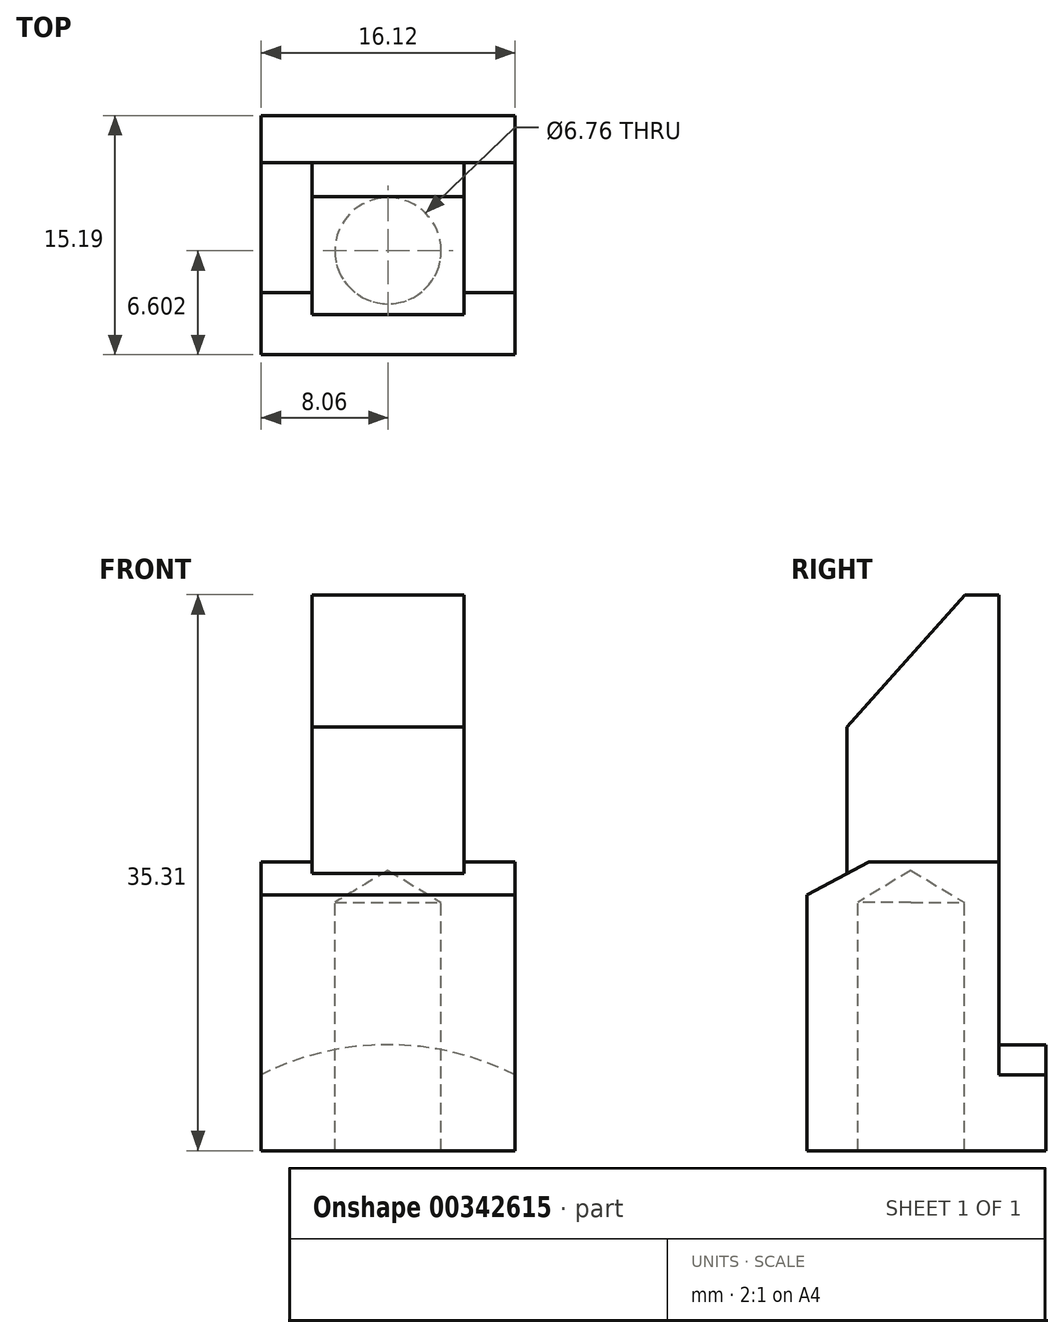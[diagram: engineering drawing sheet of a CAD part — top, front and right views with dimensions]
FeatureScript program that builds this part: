
annotation { "Feature Type Name" : "Feature", "Feature Type Description" : "" }
export const myFeature = defineFeature(function(context is Context, id is Id, definition is map)
    precondition{}
    {
        {
            var Q0;
            Q0=qCreatedBy(makeId("Front.planeOp"),FACE);
            var sketch = newSketch(context, id + "F0", { "sketchPlane" : qUnion([Q0])});
            skLineSegment(sketch, "E0.bottom", {"start": v(-4.83, 35.3) * mm, "end": v(4.83, 35.3) * mm});
            skLineSegment(sketch, "E0.top", {"start": v(-8.06, 0) * mm, "end": v(8.06, 0) * mm});
            skLineSegment(sketch, "E0.left", {"start": v(-8.06, 18.34) * mm, "end": v(-8.06, 0) * mm});
            skLineSegment(sketch, "E0.right", {"start": v(8.06, 18.34) * mm, "end": v(8.06, 0) * mm});
            skLineSegment(sketch, "E1", {"start": v(-8.06, 18.34) * mm, "end": v(8.06, 18.34) * mm});
            skLineSegment(sketch, "E2", {"start": v(4.83, 35.3) * mm, "end": v(4.83, 18.34) * mm});
            skLineSegment(sketch, "E3", {"start": v(-4.83, 35.3) * mm, "end": v(-4.83, 18.34) * mm});
            skLineSegment(sketch, "E4", {"start": v(-4.83, 35.3) * mm, "end": v(4.83, 18.34) * mm, "construction": true});
            skLineSegment(sketch, "E5", {"start": v(0, 26.82) * mm, "end": v(0, 0) * mm, "construction": true});
            skPoint(sketch, "E5.startSnap0", {"position": v(0, 26.82) * mm});
            skArc(sketch, "E6", {"start": v(8.06, 4.83) * mm, "mid": v(0, 6.73) * mm, "end": v(-8.06, 4.83) * mm});
            skLineSegment(sketch, "E7", {"start": v(0, 0) * mm, "end": v(0, -11.3) * mm, "construction": true});
            skSolve(sketch);
        }
        {
            var Q0;
            Q0 = qSketchRegion(id + "F0", true);
            extrude(context, id + "F1", {"entities" : qUnion([Q0]), "depth" : 12.2 * mm});
        }
        {
            var Q0;
            {var subQ0=sQuery(id+"F0.wireOp",EDGE,"E0.top");Q0=makeQuery(id+"F0.imprint","IMPRINT",FACE,{"disambiguationData":[TD([[makeQuery(id+"F0.imprint","IMPRINT",EDGE,{"derivedFrom":subQ0}),1.0]])]});}
            extrude(context, id + "F2", {"entities" : qUnion([Q0]), "operationType" : NewBodyOperationType.ADD, "oppositeDirection" : true, "depth" : 3 * mm});
        }
        {
            var Q0;
            Q0=makeQuery(id+"F1.opExtrude","SWEPT_FACE",FACE,{"disambiguationData":[OSD([sQuery(id+"F0.wireOp",EDGE,"E3")])]});
            var sketch = newSketch(context, id + "F3", { "sketchPlane" : qUnion([Q0])});
            skLineSegment(sketch, "E8", {"start": v(2.16, 35.3) * mm, "end": v(9.65, 26.92) * mm});
            skLineSegment(sketch, "E9", {"start": v(9.65, 26.92) * mm, "end": v(15.1, 26.92) * mm, "construction": true});
            skLineSegment(sketch, "E10", {"start": v(15.1, 26.92) * mm, "end": v(15.1, 37.65) * mm});
            skLineSegment(sketch, "E11", {"start": v(15.1, 37.65) * mm, "end": v(2.16, 37.65) * mm});
            skLineSegment(sketch, "E12", {"start": v(2.16, 37.65) * mm, "end": v(2.16, 35.3) * mm});
            skLineSegment(sketch, "E13", {"start": v(9.65, 26.92) * mm, "end": v(9.65, 17.6) * mm});
            skLineSegment(sketch, "E14", {"start": v(9.65, 17.6) * mm, "end": v(12.2, 16.26) * mm});
            skLineSegment(sketch, "E15", {"start": v(9.65, 17.6) * mm, "end": v(8.26, 18.34) * mm});
            skLineSegment(sketch, "E16", {"start": v(12.2, 16.26) * mm, "end": v(15.1, 16.26) * mm});
            skLineSegment(sketch, "E17", {"start": v(15.1, 16.26) * mm, "end": v(15.1, 26.92) * mm});
            skLineSegment(sketch, "E18.0", {"start": v(12.2, 18.34) * mm, "end": v(12.2, 0) * mm, "construction": true});
            skSolve(sketch);
        }
        {
            var Q0;
            Q0 = qSketchRegion(id + "F3", true);
            extrude(context, id + "F4", {"entities" : qUnion([Q0]), "operationType" : NewBodyOperationType.REMOVE, "oppositeDirection" : true, "depth" : 50.8 * mm, "symmetric" : true});
        }
        {
            var Q0;
            {var subQ3=sQuery(id+"F3.wireOp",EDGE,"E8");Q0=makeQuery(id+"F3.imprint","IMPRINT",FACE,{"disambiguationData":[TD([[makeQuery(id+"F3.imprint","IMPRINT",EDGE,{"derivedFrom":subQ3}),-1.0]])]});}
            var sketch = newSketch(context, id + "F5", { "sketchPlane" : qUnion([Q0])});
            skLineSegment(sketch, "E19.0", {"start": v(9.65, 18.34) * mm, "end": v(8.26, 18.34) * mm});
            skPoint(sketch, "E20.0", {"position": v(8.95, 17.97) * mm});
            skLineSegment(sketch, "E21.0", {"start": v(9.65, 18.34) * mm, "end": v(9.65, 17.6) * mm});
            skPoint(sketch, "E22.orphan", {"position": v(9.65, 26.92) * mm});
            skLineSegment(sketch, "E23.0", {"start": v(9.65, 17.6) * mm, "end": v(8.26, 18.34) * mm});
            skPoint(sketch, "E24.orphan", {"position": v(0, 18.34) * mm});
            skSolve(sketch);
        }
        {
            var Q0;
            Q0 = qSketchRegion(id + "F5", true);
            var Q1;
            {var subQ0=sQuery(id+"F0.wireOp",EDGE,"E0.left");Q1=makeQuery(id+"F2.boolean.opBoolean","MERGE",FACE,{"derivedFrom":[makeQuery(id+"F1.opExtrude","SWEPT_FACE",FACE,{"disambiguationData":[OSD([subQ0])]}),makeQuery(id+"F2.opExtrude","SWEPT_FACE",FACE,{"disambiguationData":[OSD([subQ0])]})]});}
            extrude(context, id + "F6", {"entities" : qUnion([Q0]), "operationType" : NewBodyOperationType.REMOVE, "endBound" : BoundingType.UP_TO_SURFACE, "endBoundEntityFace" : qUnion([Q1]), "depth" : 25.4 * mm});
        }
        {
            var Q0;
            Q0=makeQuery(id+"F1.opExtrude","SWEPT_FACE",FACE,{"disambiguationData":[OSD([sQuery(id+"F0.wireOp",EDGE,"E2")])]});
            var sketch = newSketch(context, id + "F7", { "sketchPlane" : qUnion([Q0])});
            skLineSegment(sketch, "E25.0", {"start": v(-9.65, 18.34) * mm, "end": v(-8.26, 18.34) * mm});
            skLineSegment(sketch, "E26.0", {"start": v(-9.65, 17.6) * mm, "end": v(-8.26, 18.34) * mm});
            skLineSegment(sketch, "E27.0", {"start": v(-9.65, 18.34) * mm, "end": v(-9.65, 17.6) * mm});
            skPoint(sketch, "E28.orphan", {"position": v(-9.65, 26.92) * mm});
            skPoint(sketch, "E29.orphan", {"position": v(0, 18.34) * mm});
            skSolve(sketch);
        }
        {
            var Q0;
            Q0=makeQuery(id+"F7.imprint","IMPRINT",FACE,{"disambiguationData":[TD([[makeQuery(id+"F7.imprint","IMPRINT",EDGE,{"derivedFrom":sQuery(id+"F7.wireOp",EDGE,"E25.0")}),-1.0]])]});
            var Q1;
            {var subQ0=sQuery(id+"F0.wireOp",EDGE,"E0.right");Q1=makeQuery(id+"F2.boolean.opBoolean","MERGE",FACE,{"derivedFrom":[makeQuery(id+"F1.opExtrude","SWEPT_FACE",FACE,{"disambiguationData":[OSD([subQ0])]}),makeQuery(id+"F2.opExtrude","SWEPT_FACE",FACE,{"disambiguationData":[OSD([subQ0])]})]});}
            extrude(context, id + "F8", {"entities" : qUnion([Q0]), "operationType" : NewBodyOperationType.REMOVE, "endBound" : BoundingType.UP_TO_SURFACE, "endBoundEntityFace" : qUnion([Q1]), "depth" : 25.4 * mm});
        }
        {
            var Q0;
            {var subQ0=sQuery(id+"F0.wireOp",EDGE,"E0.top");Q0=makeQuery(id+"F2.boolean.opBoolean","MERGE",FACE,{"derivedFrom":[makeQuery(id+"F1.opExtrude","SWEPT_FACE",FACE,{"disambiguationData":[OSD([subQ0])]}),makeQuery(id+"F2.opExtrude","SWEPT_FACE",FACE,{"disambiguationData":[OSD([subQ0])]})]});}
            var sketch = newSketch(context, id + "F9", { "sketchPlane" : qUnion([Q0])});
            skLineSegment(sketch, "E30", {"start": v(0, 12.2) * mm, "end": v(0, -3) * mm, "construction": true});
            skCircle(sketch, "E31", {"center": v(0, 5.59) * mm, "radius": 3.43 * mm});
            skSolve(sketch);
        }
        {
            var Q0;
            Q0=sQuery(id+"F9.wireOp",VERTEX,"E31.center");
            var Q1;
            Q1=makeQuery(id+"F1.opExtrude","SWEPT_BODY",BODY,{"disambiguationData":[OSD([sQuery(id+"F0.wireOp",EDGE,"E0.bottom"),sQuery(id+"F0.wireOp",EDGE,"E0.top"),sQuery(id+"F0.wireOp",EDGE,"E0.left"),sQuery(id+"F0.wireOp",EDGE,"E0.right"),sQuery(id+"F0.wireOp",EDGE,"E1"),sQuery(id+"F0.wireOp",EDGE,"E2"),sQuery(id+"F0.wireOp",EDGE,"E3")])]});
            hole(context, id + "F10", {"style" : HoleStyle.SIMPLE, "endStyle" : HoleEndStyle.BLIND, "standardTappedOrClearance" : lookupTablePath({ "standard" : "ANSI", "fit" : "Normal (ASME)", "size" : "1/4", "type" : "Clearance" }), "standardBlindInLast" : lookupTablePath({ "fit" : "Free", "standard" : "ANSI", "size" : "1/4", "type" : "Clearance" }), "holeDiameter" : 6.76 * mm, "holeDepth" : 15.77 * mm, "isTappedThrough" : true, "tappedDepth" : 12.7 * mm, "tapClearance" : 3, "locations" : qUnion([Q0]), "scope" : qUnion([Q1]), "startStyle" : HoleStartStyle.PART});
        }
    });
